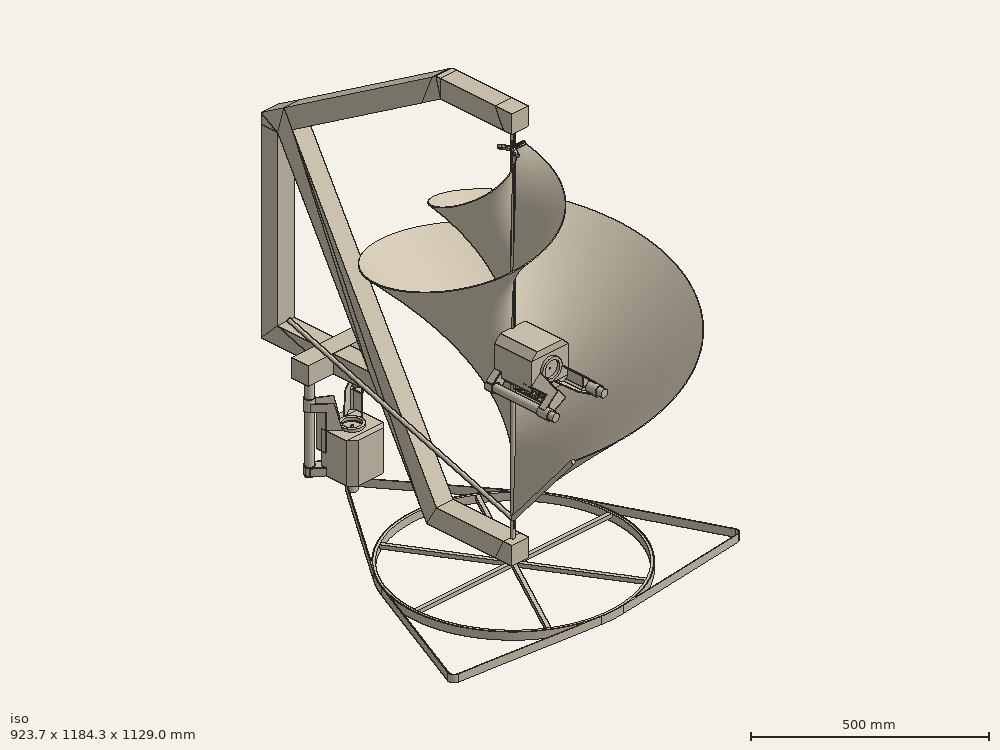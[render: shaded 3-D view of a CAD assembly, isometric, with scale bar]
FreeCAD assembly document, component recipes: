
FREECAD ASSEMBLY — COMPONENT RECIPES ("BASE Con motor")

This assembly document has 6 components, labeled P0..P5 below (a component is one placed body or linked part). 0 of them carry a construction recipe — the FreeCAD feature program that regenerates the part from scratch, quoted from this document or its linked companion documents; the rest are supplied as boundary geometry only. No exploded tour is included for this assembly.
COMPONENT P0 — geometry summary ("Sweep002"; no construction recipe available for this part):
  bounding box: 1000.0 x 10.0 x 10.0 mm
  tessellated surface: 360 triangles
  volume: 78540 mm^3 (79% of its bounding box)
  symmetry: 2-fold rotationally symmetric about the x axis; 2-fold rotationally symmetric about the y axis; revolution-symmetric about the z axis through its bounding-box center; mirror-symmetric across its x mid-plane, y mid-plane, z mid-plane
COMPONENT P1 — geometry summary ("Extrude050"; no construction recipe available for this part):
  bounding box: 30.0 x 25.0 x 25.0 mm
  tessellated surface: 500 triangles
  volume: 14726 mm^3 (79% of its bounding box)
  symmetry: 2-fold rotationally symmetric about the x axis; revolution-symmetric about the y axis through its bounding-box center; 2-fold rotationally symmetric about the z axis; mirror-symmetric across its y mid-plane
COMPONENT P2 — geometry summary ("Extrude051"; no construction recipe available for this part):
  bounding box: 157.0 x 5.0 x 5.0 mm
  tessellated surface: 180 triangles
  volume: 3083 mm^3 (79% of its bounding box)
  symmetry: 2-fold rotationally symmetric about the x axis; revolution-symmetric about the y axis through its bounding-box center; 2-fold rotationally symmetric about the z axis; mirror-symmetric across its x mid-plane, y mid-plane, z mid-plane
COMPONENT P3 — geometry summary ("Cut003"; no construction recipe available for this part):
  bounding box: 124.0 x 110.0 x 110.0 mm
  tessellated surface: 2,296 triangles
  volume: 1274765 mm^3 (85% of its bounding box)
  symmetry: 4-fold rotationally symmetric about the y axis; mirror-symmetric across its x mid-plane, z mid-plane
COMPONENT P4 — geometry summary ("Fusion010"; no construction recipe available for this part):
  bounding box: 170.0 x 68.0 x 20.0 mm
  tessellated surface: 2,512 triangles
  volume: 26527 mm^3 (11% of its bounding box)
  symmetry: mirror-symmetric across its x mid-plane
COMPONENT P5 — geometry summary ("Fusion011"; no construction recipe available for this part):
  bounding box: 170.0 x 130.1 x 68.0 mm
  tessellated surface: 3,006 triangles
  volume: 68987 mm^3 (5% of its bounding box)
  symmetry: mirror-symmetric across its x mid-plane
PROVENANCE & LICENSES
A FreeCAD (.FCStd) document from a public repository crawl; recipes are the document's own serialized feature recipes (and, for linked parts, companion documents' recipes).
License: as declared in the source repository (recorded in the dataset sidecar).
